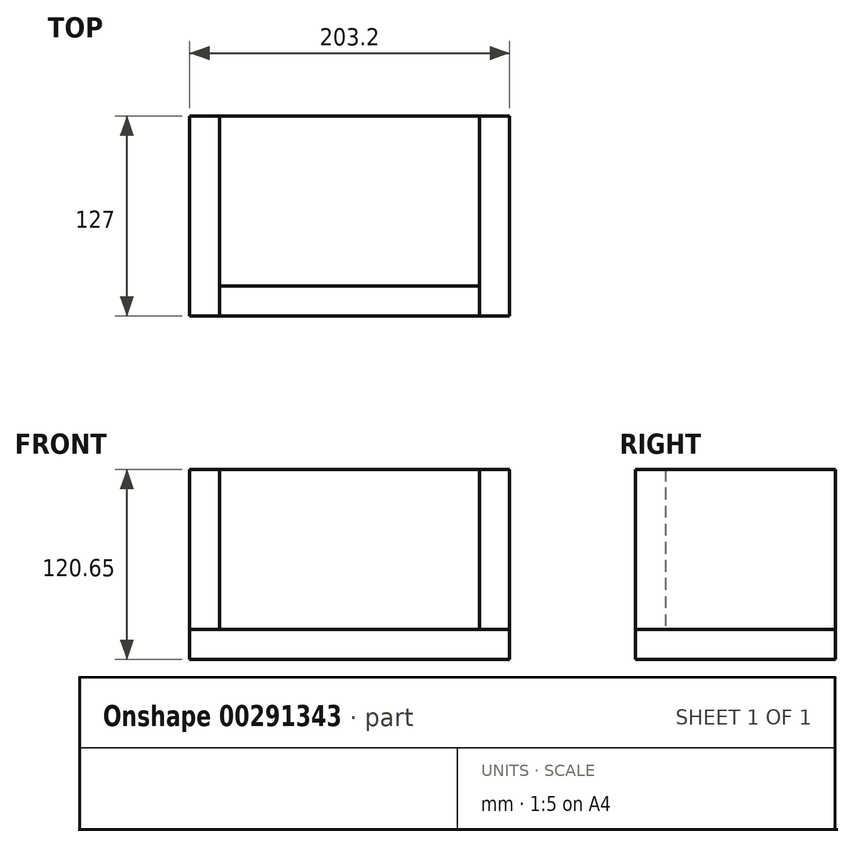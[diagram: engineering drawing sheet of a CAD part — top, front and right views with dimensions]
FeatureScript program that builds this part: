
annotation { "Feature Type Name" : "Feature", "Feature Type Description" : "" }
export const myFeature = defineFeature(function(context is Context, id is Id, definition is map)
    precondition{}
    {
        {
            var Q0;
            Q0=qCreatedBy(makeId("Top.planeOp"),FACE);
            var sketch = newSketch(context, id + "F0", { "sketchPlane" : qUnion([Q0])});
            skLineSegment(sketch, "E0.bottom", {"start": v(101.6, -63.5) * mm, "end": v(-101.6, -63.5) * mm});
            skLineSegment(sketch, "E0.top", {"start": v(101.6, 63.5) * mm, "end": v(-101.6, 63.5) * mm});
            skLineSegment(sketch, "E0.left", {"start": v(101.6, -63.5) * mm, "end": v(101.6, 63.5) * mm});
            skLineSegment(sketch, "E0.right", {"start": v(-101.6, -63.5) * mm, "end": v(-101.6, 63.5) * mm});
            skPoint(sketch, "E0.middle", {"position": v(0, 0) * mm});
            skSolve(sketch);
        }
        {
            var Q0;
            Q0 = qSketchRegion(id + "F0", true);
            extrude(context, id + "F1", {"entities" : qUnion([Q0]), "depth" : 19.05 * mm});
        }
        {
            var Q0;
            Q0=makeQuery(id+"F1.opExtrude","CAP_FACE",FACE,{"disambiguationData":[OSD([sQuery(id+"F0.wireOp",EDGE,"E0.bottom"),sQuery(id+"F0.wireOp",EDGE,"E0.top"),sQuery(id+"F0.wireOp",EDGE,"E0.left"),sQuery(id+"F0.wireOp",EDGE,"E0.right")])],"isStart":false});
            var sketch = newSketch(context, id + "F2", { "sketchPlane" : qUnion([Q0])});
            skLineSegment(sketch, "E1.bottom", {"start": v(-101.6, -63.5) * mm, "end": v(-82.55, -63.5) * mm});
            skLineSegment(sketch, "E1.top", {"start": v(-101.6, 63.5) * mm, "end": v(-82.55, 63.5) * mm});
            skLineSegment(sketch, "E1.left", {"start": v(-101.6, -63.5) * mm, "end": v(-101.6, 63.5) * mm});
            skLineSegment(sketch, "E1.right", {"start": v(-82.55, -63.5) * mm, "end": v(-82.55, 63.5) * mm});
            skLineSegment(sketch, "E2.bottom", {"start": v(82.55, -63.5) * mm, "end": v(101.6, -63.5) * mm});
            skLineSegment(sketch, "E2.top", {"start": v(82.55, 63.5) * mm, "end": v(101.6, 63.5) * mm});
            skLineSegment(sketch, "E2.left", {"start": v(82.55, -63.5) * mm, "end": v(82.55, 63.5) * mm});
            skLineSegment(sketch, "E2.right", {"start": v(101.6, -63.5) * mm, "end": v(101.6, 63.5) * mm});
            skSolve(sketch);
        }
        {
            var Q0;
            Q0 = qSketchRegion(id + "F2", true);
            extrude(context, id + "F3", {"entities" : qUnion([Q0]), "depth" : 101.6 * mm});
        }
        {
            var Q0;
            Q0=makeQuery(id+"F1.opExtrude","CAP_FACE",FACE,{"disambiguationData":[OSD([sQuery(id+"F0.wireOp",EDGE,"E0.bottom"),sQuery(id+"F0.wireOp",EDGE,"E0.top"),sQuery(id+"F0.wireOp",EDGE,"E0.left"),sQuery(id+"F0.wireOp",EDGE,"E0.right")])],"isStart":false});
            var sketch = newSketch(context, id + "F4", { "sketchPlane" : qUnion([Q0])});
            skLineSegment(sketch, "E3.bottom", {"start": v(-82.55, -63.5) * mm, "end": v(82.55, -63.5) * mm});
            skLineSegment(sketch, "E3.top", {"start": v(-82.55, -44.45) * mm, "end": v(82.55, -44.45) * mm});
            skLineSegment(sketch, "E3.left", {"start": v(-82.55, -63.5) * mm, "end": v(-82.55, -44.45) * mm});
            skLineSegment(sketch, "E3.right", {"start": v(82.55, -63.5) * mm, "end": v(82.55, -44.45) * mm});
            skSolve(sketch);
        }
        {
            var Q0;
            Q0 = qSketchRegion(id + "F4", true);
            var Q1;
            Q1=makeQuery(id+"F3.opExtrude","CAP_FACE",FACE,{"disambiguationData":[OSD([sQuery(id+"F2.wireOp",EDGE,"E2.bottom"),sQuery(id+"F2.wireOp",EDGE,"E2.top"),sQuery(id+"F2.wireOp",EDGE,"E2.left"),sQuery(id+"F2.wireOp",EDGE,"E2.right")])],"isStart":false});
            extrude(context, id + "F5", {"entities" : qUnion([Q0]), "endBound" : BoundingType.UP_TO_SURFACE, "endBoundEntityFace" : qUnion([Q1]), "depth" : 25.4 * mm});
        }
    });
